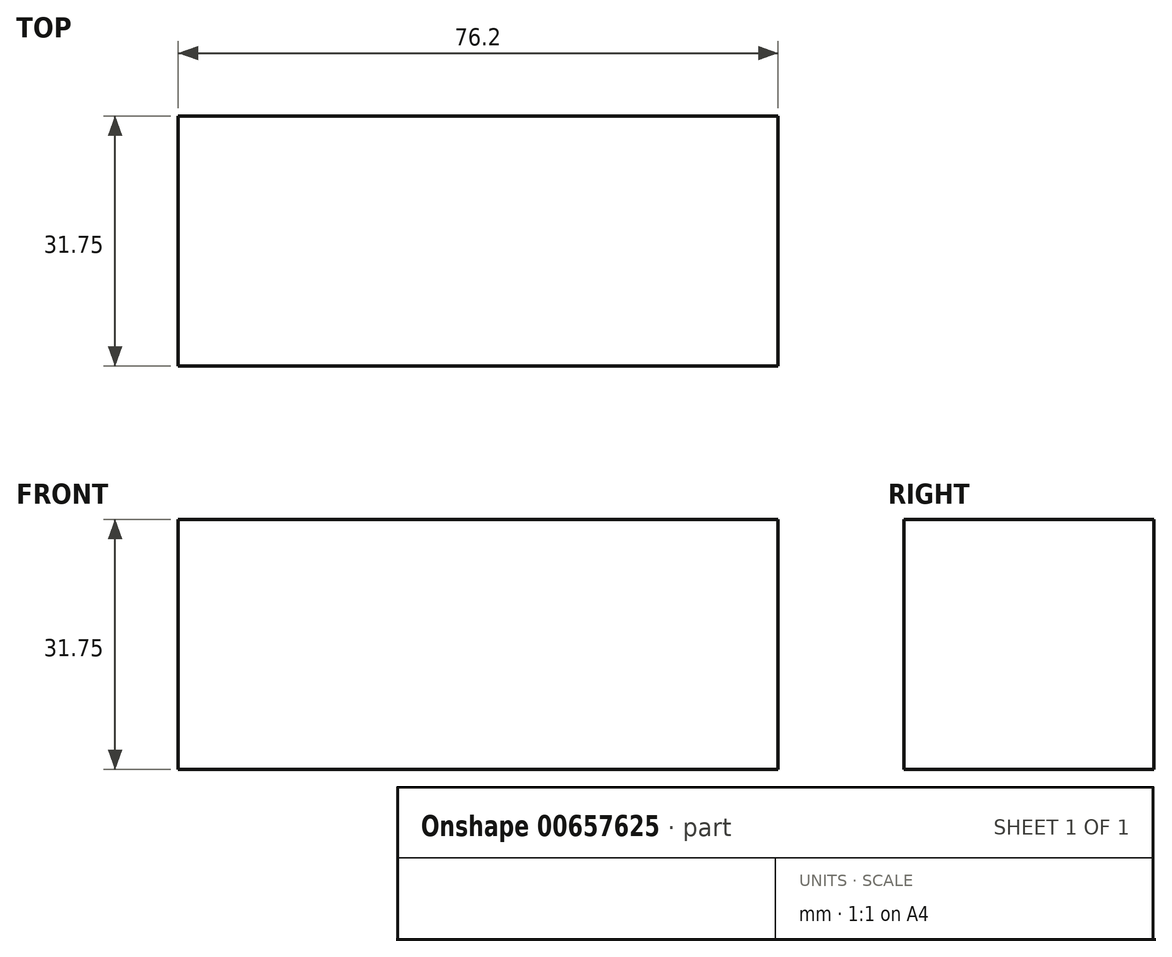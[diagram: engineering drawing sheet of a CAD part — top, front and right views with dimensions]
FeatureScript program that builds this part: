
annotation { "Feature Type Name" : "Feature", "Feature Type Description" : "" }
export const myFeature = defineFeature(function(context is Context, id is Id, definition is map)
    precondition{}
    {
        {
            var Q0;
            Q0=qCreatedBy(makeId("Top.planeOp"),FACE);
            var sketch = newSketch(context, id + "F0", { "sketchPlane" : qUnion([Q0])});
            skLineSegment(sketch, "E0.bottom", {"start": v(0, 0) * mm, "end": v(76.2, 0) * mm});
            skLineSegment(sketch, "E0.top", {"start": v(0, -31.75) * mm, "end": v(76.2, -31.75) * mm});
            skLineSegment(sketch, "E0.left", {"start": v(0, 0) * mm, "end": v(0, -31.75) * mm});
            skLineSegment(sketch, "E0.right", {"start": v(76.2, 0) * mm, "end": v(76.2, -31.75) * mm});
            skSolve(sketch);
        }
        {
            var Q0;
            Q0=makeQuery(id+"F0.imprint","IMPRINT",FACE,{"disambiguationData":[TD([[makeQuery(id+"F0.imprint","IMPRINT",EDGE,{"derivedFrom":sQuery(id+"F0.wireOp",EDGE,"E0.bottom")}),-1.0]])]});
            extrude(context, id + "F1", {"entities" : qUnion([Q0]), "depth" : 31.75 * mm, "offsetDistance" : 25.4 * mm});
        }
    });
